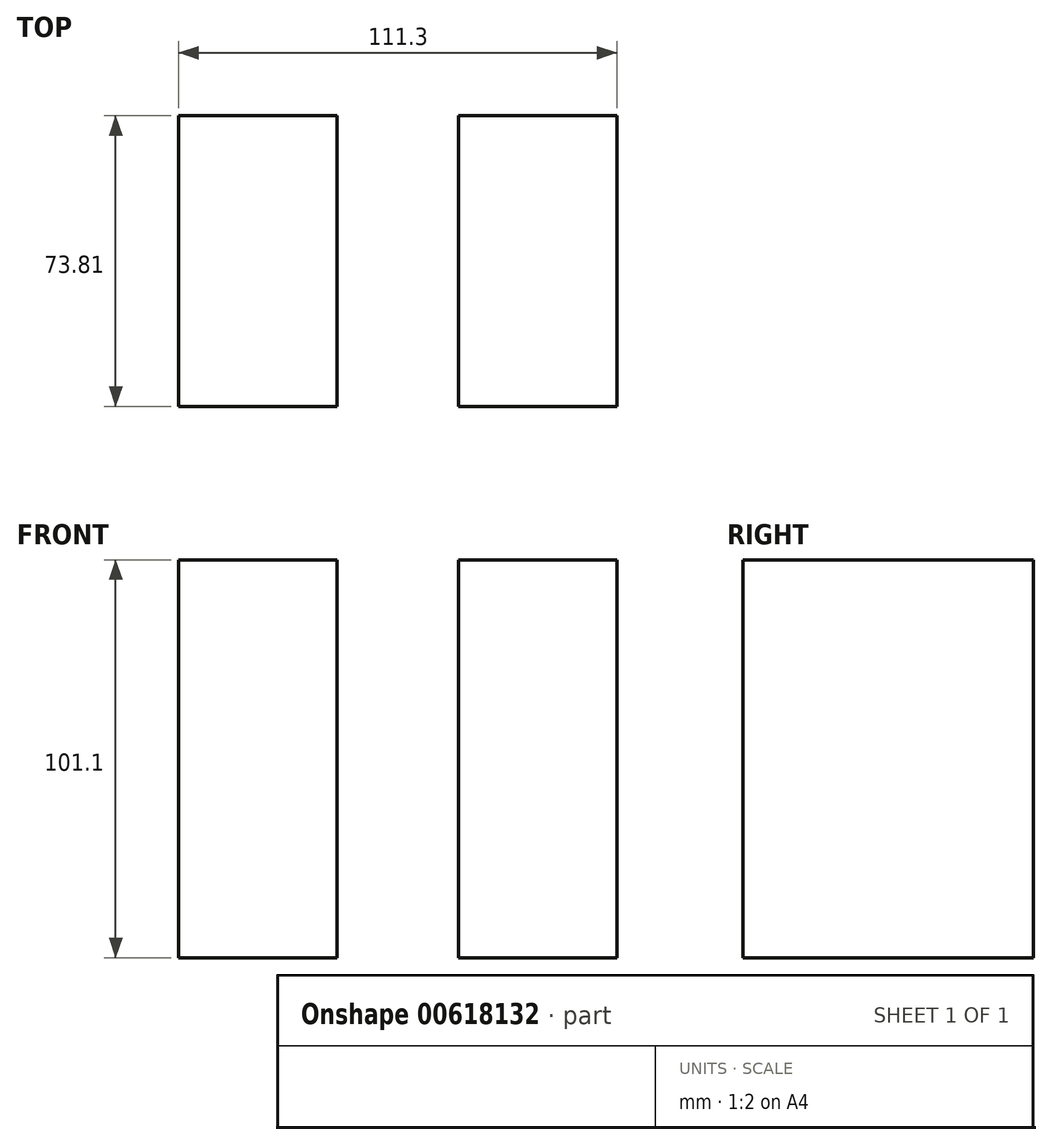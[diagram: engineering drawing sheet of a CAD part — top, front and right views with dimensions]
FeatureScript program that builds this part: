
annotation { "Feature Type Name" : "Feature", "Feature Type Description" : "" }
export const myFeature = defineFeature(function(context is Context, id is Id, definition is map)
    precondition{}
    {
        {
            var Q0;
            Q0=qCreatedBy(makeId("Front.planeOp"),FACE);
            var sketch = newSketch(context, id + "F0", { "sketchPlane" : qUnion([Q0])});
            skLineSegment(sketch, "E0.bottom", {"start": v(-55.65, 50.97) * mm, "end": v(-15.39, 50.97) * mm});
            skLineSegment(sketch, "E0.top", {"start": v(-55.65, -50.13) * mm, "end": v(-15.39, -50.13) * mm});
            skLineSegment(sketch, "E0.left", {"start": v(-55.65, 50.97) * mm, "end": v(-55.65, -50.13) * mm});
            skLineSegment(sketch, "E0.right", {"start": v(-15.39, 50.97) * mm, "end": v(-15.39, -50.13) * mm});
            skSolve(sketch);
        }
        {
            var Q0;
            Q0=makeQuery(id+"F0.imprint","IMPRINT",FACE,{"disambiguationData":[TD([[makeQuery(id+"F0.imprint","IMPRINT",EDGE,{"derivedFrom":sQuery(id+"F0.wireOp",EDGE,"E0.bottom")}),-1.0]])]});
            extrude(context, id + "F1", {"entities" : qUnion([Q0]), "depth" : 73.81 * mm, "offsetDistance" : 25.4 * mm});
        }
        {
            var Q0;
            Q0=makeQuery(id+"F1.opExtrude","SWEPT_BODY",BODY,{"disambiguationData":[OSD([sQuery(id+"F0.wireOp",EDGE,"E0.bottom"),sQuery(id+"F0.wireOp",EDGE,"E0.top"),sQuery(id+"F0.wireOp",EDGE,"E0.left"),sQuery(id+"F0.wireOp",EDGE,"E0.right")])]});
            var Q1;
            Q1=qCreatedBy(makeId("Right.planeOp"),FACE);
            mirror(context, id + "F2", {"entities" : qUnion([Q0]), "mirrorPlane" : qUnion([Q1])});
        }
    });
